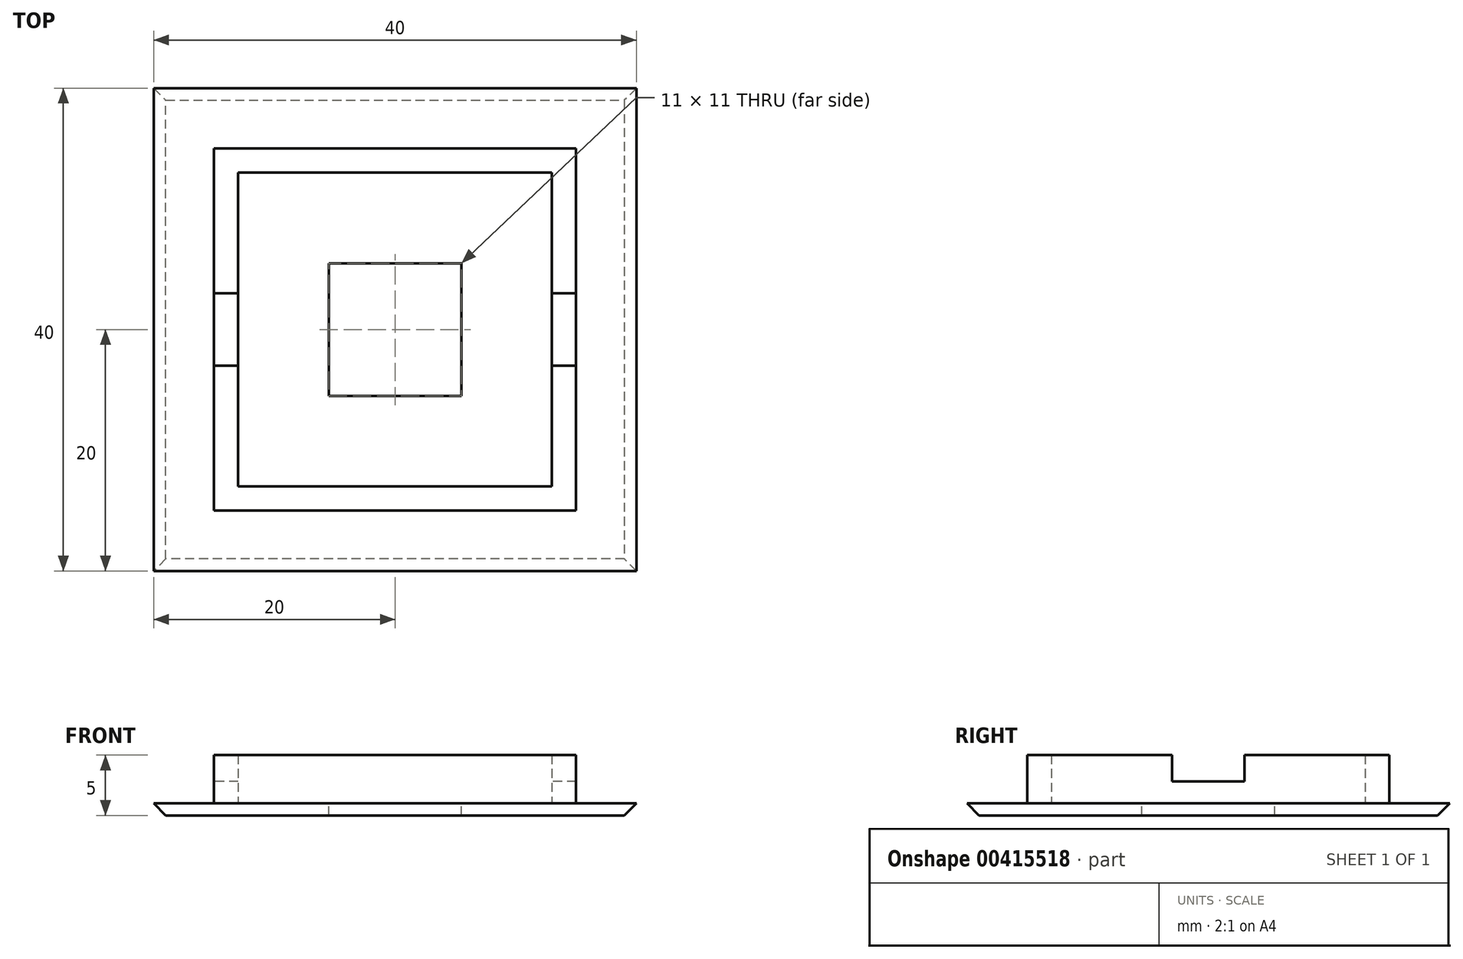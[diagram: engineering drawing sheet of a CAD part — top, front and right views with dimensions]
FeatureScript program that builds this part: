
annotation { "Feature Type Name" : "Feature", "Feature Type Description" : "" }
export const myFeature = defineFeature(function(context is Context, id is Id, definition is map)
    precondition{}
    {
        {
            var Q0;
            Q0=qCreatedBy(makeId("Top.planeOp"),FACE);
            var sketch = newSketch(context, id + "F0", { "sketchPlane" : qUnion([Q0])});
            skLineSegment(sketch, "E0.bottom", {"start": v(15, -15) * mm, "end": v(-15, -15) * mm});
            skLineSegment(sketch, "E0.top", {"start": v(15, 15) * mm, "end": v(-15, 15) * mm});
            skLineSegment(sketch, "E0.left", {"start": v(15, -15) * mm, "end": v(15, 15) * mm});
            skLineSegment(sketch, "E0.right", {"start": v(-15, -15) * mm, "end": v(-15, 15) * mm});
            skPoint(sketch, "E0.middle", {"position": v(0, 0) * mm});
            skLineSegment(sketch, "E1.0", {"start": v(13, -13) * mm, "end": v(-13, -13) * mm});
            skLineSegment(sketch, "E1.1", {"start": v(13, -13) * mm, "end": v(13, 13) * mm});
            skLineSegment(sketch, "E1.2", {"start": v(13, 13) * mm, "end": v(-13, 13) * mm});
            skLineSegment(sketch, "E1.3", {"start": v(-13, -13) * mm, "end": v(-13, 13) * mm});
            skLineSegment(sketch, "E2.0", {"start": v(-20, -20) * mm, "end": v(-20, 20) * mm});
            skLineSegment(sketch, "E2.1", {"start": v(20, -20) * mm, "end": v(-20, -20) * mm});
            skLineSegment(sketch, "E2.2", {"start": v(20, -20) * mm, "end": v(20, 20) * mm});
            skLineSegment(sketch, "E2.3", {"start": v(20, 20) * mm, "end": v(-20, 20) * mm});
            skSolve(sketch);
        }
        {
            var Q0;
            Q0=makeQuery(id+"F0.imprint","IMPRINT",FACE,{"disambiguationData":[TD([[makeQuery(id+"F0.imprint","IMPRINT",EDGE,{"derivedFrom":sQuery(id+"F0.wireOp",EDGE,"E0.bottom")}),-1.0]])]});
            extrude(context, id + "F1", {"entities" : qUnion([Q0]), "depth" : 5 * mm});
        }
        {
            var Q0;
            Q0 = qSketchRegion(id + "F0", true);
            var Q1;
            Q1=makeQuery(id+"F0.imprint","IMPRINT",FACE,{"disambiguationData":[TD([[makeQuery(id+"F0.imprint","IMPRINT",EDGE,{"derivedFrom":sQuery(id+"F0.wireOp",EDGE,"E1.0")}),-1.0]])]});
            extrude(context, id + "F2", {"entities" : qUnion([Q0, Q1]), "operationType" : NewBodyOperationType.ADD, "depth" : 1 * mm});
        }
        {
            var Q0;
            Q0=makeQuery(id+"F1.opExtrude","CAP_FACE",FACE,{"disambiguationData":[OSD([sQuery(id+"F0.wireOp",EDGE,"E0.bottom"),sQuery(id+"F0.wireOp",EDGE,"E0.top"),sQuery(id+"F0.wireOp",EDGE,"E0.left"),sQuery(id+"F0.wireOp",EDGE,"E0.right"),sQuery(id+"F0.wireOp",EDGE,"E1.0"),sQuery(id+"F0.wireOp",EDGE,"E1.1"),sQuery(id+"F0.wireOp",EDGE,"E1.2"),sQuery(id+"F0.wireOp",EDGE,"E1.3")])],"isStart":false});
            var sketch = newSketch(context, id + "F3", { "sketchPlane" : qUnion([Q0])});
            skLineSegment(sketch, "E3.bottom", {"start": v(15, -3) * mm, "end": v(-15, -3) * mm});
            skLineSegment(sketch, "E3.top", {"start": v(15, 3) * mm, "end": v(-15, 3) * mm});
            skLineSegment(sketch, "E3.left", {"start": v(15, -3) * mm, "end": v(15, 3) * mm});
            skLineSegment(sketch, "E3.right", {"start": v(-15, -3) * mm, "end": v(-15, 3) * mm});
            skPoint(sketch, "E3.middle", {"position": v(0, 0) * mm});
            skSolve(sketch);
        }
        {
            var Q0;
            {var subQ0=sQuery(id+"F3.wireOp",EDGE,"E3.right");Q0=makeQuery(id+"F3.imprint","IMPRINT",FACE,{"disambiguationData":[TD([[makeQuery(id+"F3.imprint","IMPRINT",EDGE,{"derivedFrom":subQ0}),-1.0]])]});}
            var Q1;
            {var subQ0=sQuery(id+"F3.wireOp",EDGE,"E3.bottom");var subQ1=makeQuery(id+"F1.opExtrude","CAP_EDGE",EDGE,{"disambiguationData":[OSD([sQuery(id+"F0.wireOp",EDGE,"E1.1")])],"isStart":false});var subQ2=makeQuery(id+"F3.imprint","INTERSECT",VERTEX,{"derivedFrom":[subQ1,subQ0]});Q1=makeQuery(id+"F3.imprint","IMPRINT",FACE,{"disambiguationData":[TD([[makeQuery(id+"F3.imprint","IMPRINT",EDGE,{"disambiguationData":[TD([[subQ2,-1.0]])],"derivedFrom":subQ0}),-1.0]])]});}
            var Q2;
            {var subQ0=sQuery(id+"F3.wireOp",EDGE,"E3.left");Q2=makeQuery(id+"F3.imprint","IMPRINT",FACE,{"disambiguationData":[TD([[makeQuery(id+"F3.imprint","IMPRINT",EDGE,{"derivedFrom":subQ0}),1.0]])]});}
            extrude(context, id + "F4", {"entities" : qUnion([Q0, Q1, Q2]), "operationType" : NewBodyOperationType.REMOVE, "oppositeDirection" : true, "depth" : 2.2 * mm});
        }
        {
            var Q0;
            Q0=makeQuery(id+"F2.opExtrude","CAP_FACE",FACE,{"disambiguationData":[OSD([sQuery(id+"F0.wireOp",EDGE,"E1.0"),sQuery(id+"F0.wireOp",EDGE,"E1.1"),sQuery(id+"F0.wireOp",EDGE,"E1.2"),sQuery(id+"F0.wireOp",EDGE,"E1.3")])],"isStart":false});
            var sketch = newSketch(context, id + "F5", { "sketchPlane" : qUnion([Q0])});
            skLineSegment(sketch, "E4.bottom", {"start": v(5.5, -5.5) * mm, "end": v(-5.5, -5.5) * mm});
            skLineSegment(sketch, "E4.top", {"start": v(5.5, 5.5) * mm, "end": v(-5.5, 5.5) * mm});
            skLineSegment(sketch, "E4.left", {"start": v(5.5, -5.5) * mm, "end": v(5.5, 5.5) * mm});
            skLineSegment(sketch, "E4.right", {"start": v(-5.5, -5.5) * mm, "end": v(-5.5, 5.5) * mm});
            skPoint(sketch, "E4.middle", {"position": v(0, 0) * mm});
            skSolve(sketch);
        }
        {
            var Q0;
            {var subQ0=sQuery(id+"F0.wireOp",EDGE,"E1.3");var subQ1=sQuery(id+"F0.wireOp",EDGE,"E1.2");var subQ2=sQuery(id+"F0.wireOp",EDGE,"E1.1");var subQ3=sQuery(id+"F0.wireOp",EDGE,"E1.0");var subQ4=sQuery(id+"F0.wireOp",EDGE,"E0.right");var subQ5=sQuery(id+"F0.wireOp",EDGE,"E0.left");var subQ6=sQuery(id+"F0.wireOp",EDGE,"E0.top");var subQ7=sQuery(id+"F0.wireOp",EDGE,"E0.bottom");Q0=makeQuery(id+"F2.boolean.opBoolean","MERGE",FACE,{"derivedFrom":[makeQuery(id+"F1.opExtrude","CAP_FACE",FACE,{"disambiguationData":[OSD([subQ7,subQ6,subQ5,subQ4,subQ3,subQ2,subQ1,subQ0])],"isStart":true}),makeQuery(id+"F2.opExtrude","CAP_FACE",FACE,{"disambiguationData":[OSD([subQ7,subQ6,subQ5,subQ4,sQuery(id+"F0.wireOp",EDGE,"E2.0"),sQuery(id+"F0.wireOp",EDGE,"E2.1"),sQuery(id+"F0.wireOp",EDGE,"E2.2"),sQuery(id+"F0.wireOp",EDGE,"E2.3")])],"isStart":true}),makeQuery(id+"F2.opExtrude","CAP_FACE",FACE,{"disambiguationData":[OSD([subQ3,subQ2,subQ1,subQ0])],"isStart":true})]});}
            chamfer(context, id + "F6", {"entities" : qUnion([Q0]), "width" : 1 * mm, "tangentPropagation" : true});
        }
        {
            var Q0;
            Q0=makeQuery(id+"F5.imprint","IMPRINT",FACE,{"disambiguationData":[TD([[makeQuery(id+"F5.imprint","IMPRINT",EDGE,{"derivedFrom":sQuery(id+"F5.wireOp",EDGE,"E4.bottom")}),-1.0]])]});
            extrude(context, id + "F7", {"entities" : qUnion([Q0]), "operationType" : NewBodyOperationType.REMOVE, "oppositeDirection" : true, "depth" : 25 * mm});
        }
    });
